# Revit family: P210641KR-107_KBSD702MSS
name_source: partatom
category: Specialty Equipment
units: mm (PartAtom-declared; Revit-internal decimal feet)

## family parameters
Always vertical = Yes
Cut with Voids When Loaded = No
Enable Cutting in Views = No
Maintain Annotation Orientation = No
Part Type = Normal
Room Calculation Point = No
Round Connector Dimension = Use Diameter
Shared = No
Work Plane-Based = No

## types (1)
- KBSD702MPS
    Accent Material = ARCAT - Metal - Steel - Gray - Light
    Amps = 0 A
    Back Panel = ARCAT - Metal - Steel - Aluminium
    Body Material = ARCAT - Metal - Steel - Gray
    Bottam Panel Material = ARCAT - Metal - Steel - Stainless - Black
    Clearance Material = ARCAT - Clearance
    Default Elevation = 0 "
    Depth = 42.34 "
    Description = SXS Refrigerator
Four mural double intelligent avec écran tactile, 8.6 pi3
    Display Panel Material = ARCAT - Glass - Black
    Door Frame = ARCAT - Metal - Steel - Stainless
    Door Material = ARCAT - Metal - Steel - Stainless
    Glass Material = ARCAT - Glass - Black
    Handle Material = ARCAT - Plastic - Grey
    Height = 83.38 "
    Logo Material = Stainless Steel
    Manufacturer = KitchenAid
    Model = KBSD702MPS
    Object = ARCAT - Plastic, ABS - Red
    Shade = APCT - Fbc
    Voltage = 0 V
    Width = 27.75 "

## geometry (parser evidence)
native form markers: Sweep x6
no freeform markers — native parametric forms only
